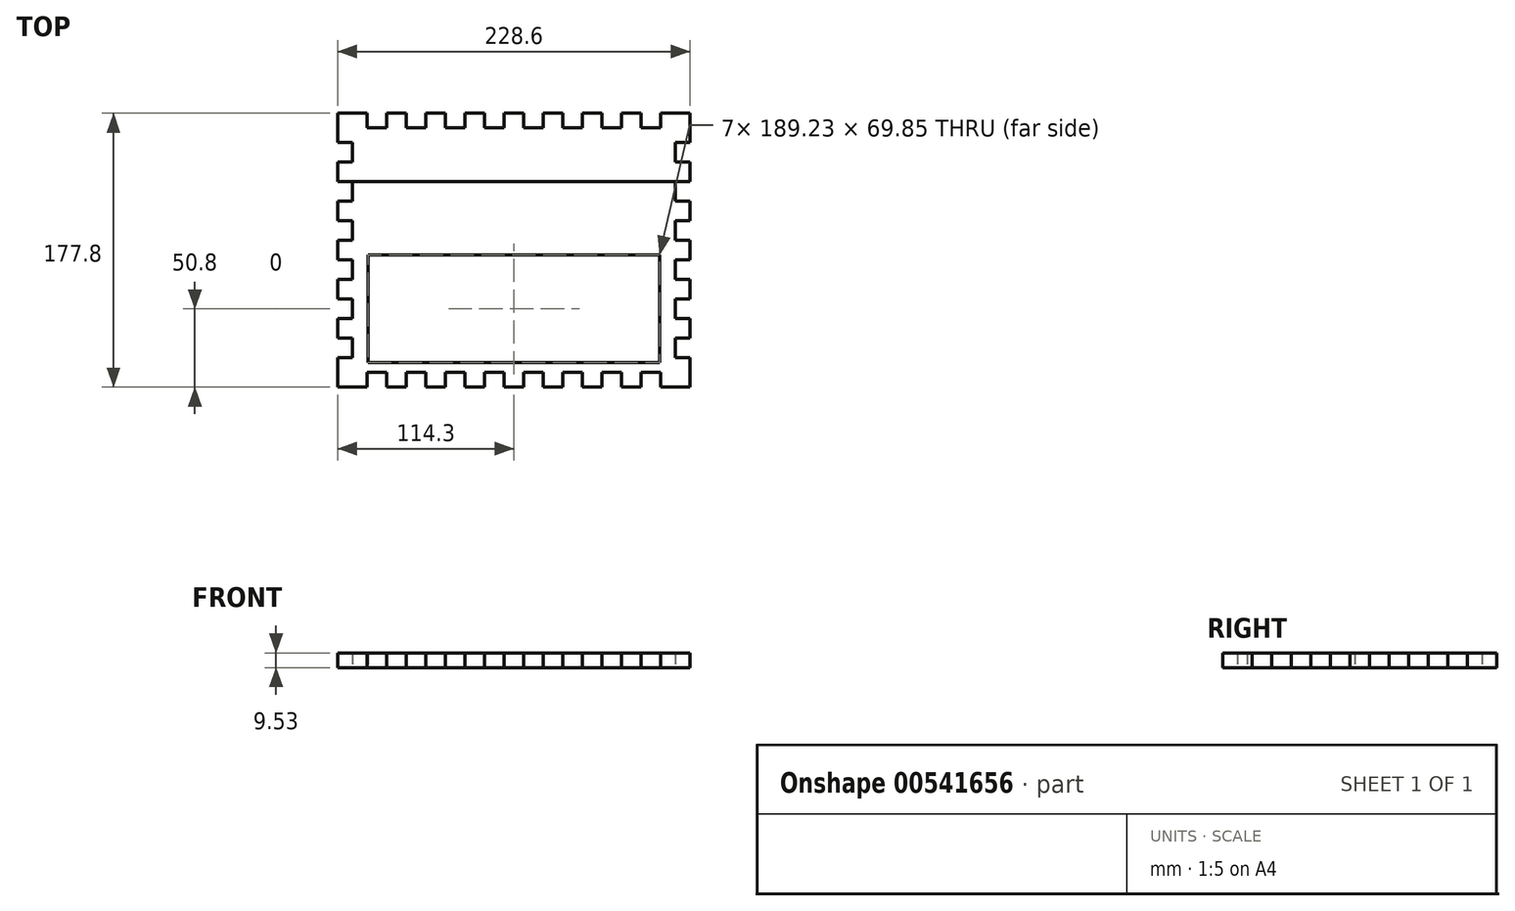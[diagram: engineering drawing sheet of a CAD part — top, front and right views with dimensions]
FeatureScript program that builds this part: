
annotation { "Feature Type Name" : "Feature", "Feature Type Description" : "" }
export const myFeature = defineFeature(function(context is Context, id is Id, definition is map)
    precondition{}
    {
        {
            var Q0;
            Q0=qCreatedBy(makeId("Top.planeOp"),FACE);
            var sketch = newSketch(context, id + "F0", { "sketchPlane" : qUnion([Q0])});
            skLineSegment(sketch, "E0.bottom", {"start": v(0, 0) * mm, "end": v(19.05, 0) * mm});
            skLineSegment(sketch, "E0.left", {"start": v(0, 0) * mm, "end": v(0, -19.05) * mm});
            skLineSegment(sketch, "E1", {"start": v(19.05, 0) * mm, "end": v(19.05, -9.53) * mm});
            skLineSegment(sketch, "E2", {"start": v(19.05, -9.53) * mm, "end": v(31.75, -9.53) * mm});
            skLineSegment(sketch, "E3", {"start": v(31.75, -9.53) * mm, "end": v(31.75, 0) * mm});
            skLineSegment(sketch, "E4", {"start": v(31.75, 0) * mm, "end": v(44.45, 0) * mm});
            skLineSegment(sketch, "E5", {"start": v(44.45, 0) * mm, "end": v(44.45, -9.52) * mm});
            skLineSegment(sketch, "E6", {"start": v(44.45, -9.52) * mm, "end": v(57.15, -9.52) * mm});
            skLineSegment(sketch, "E7", {"start": v(57.15, -9.52) * mm, "end": v(57.15, 0) * mm});
            skLineSegment(sketch, "E8.trimOffspring", {"start": v(57.15, 0) * mm, "end": v(69.85, 0) * mm});
            skLineSegment(sketch, "E9", {"start": v(69.85, 0) * mm, "end": v(69.85, -9.52) * mm});
            skLineSegment(sketch, "E10", {"start": v(69.85, -9.52) * mm, "end": v(82.55, -9.52) * mm});
            skLineSegment(sketch, "E11", {"start": v(82.55, -9.52) * mm, "end": v(82.55, 0) * mm});
            skLineSegment(sketch, "E12", {"start": v(82.55, 0) * mm, "end": v(95.25, 0) * mm});
            skLineSegment(sketch, "E13", {"start": v(95.25, 0) * mm, "end": v(95.25, -9.52) * mm});
            skLineSegment(sketch, "E14", {"start": v(95.25, -9.52) * mm, "end": v(107.95, -9.52) * mm});
            skLineSegment(sketch, "E15", {"start": v(107.95, -9.52) * mm, "end": v(107.95, 0) * mm});
            skLineSegment(sketch, "E16", {"start": v(107.95, 0) * mm, "end": v(120.65, 0) * mm});
            skLineSegment(sketch, "E17", {"start": v(120.65, 0) * mm, "end": v(120.65, -9.52) * mm});
            skLineSegment(sketch, "E18", {"start": v(120.65, -9.52) * mm, "end": v(133.35, -9.52) * mm});
            skLineSegment(sketch, "E19", {"start": v(133.35, -9.52) * mm, "end": v(133.35, 0) * mm});
            skLineSegment(sketch, "E20.trimOffspring", {"start": v(133.35, 0) * mm, "end": v(146.05, 0) * mm});
            skLineSegment(sketch, "E21", {"start": v(146.05, 0) * mm, "end": v(146.05, -9.53) * mm});
            skLineSegment(sketch, "E22", {"start": v(146.05, -9.52) * mm, "end": v(158.75, -9.52) * mm});
            skLineSegment(sketch, "E23", {"start": v(158.75, -9.53) * mm, "end": v(158.75, 0) * mm});
            skLineSegment(sketch, "E24", {"start": v(158.75, 0) * mm, "end": v(171.45, 0) * mm});
            skLineSegment(sketch, "E25", {"start": v(171.45, 0) * mm, "end": v(171.45, -9.52) * mm});
            skLineSegment(sketch, "E26", {"start": v(171.45, -9.52) * mm, "end": v(184.15, -9.52) * mm});
            skLineSegment(sketch, "E27", {"start": v(184.15, -9.52) * mm, "end": v(184.15, 0) * mm});
            skLineSegment(sketch, "E28", {"start": v(184.15, 0) * mm, "end": v(196.85, 0) * mm});
            skLineSegment(sketch, "E29", {"start": v(196.85, 0) * mm, "end": v(196.85, -9.52) * mm});
            skLineSegment(sketch, "E30", {"start": v(196.85, -9.52) * mm, "end": v(209.55, -9.52) * mm});
            skLineSegment(sketch, "E31", {"start": v(209.55, -9.52) * mm, "end": v(209.55, 0) * mm});
            skLineSegment(sketch, "E32.trimOffspring", {"start": v(209.55, 0) * mm, "end": v(228.6, 0) * mm});
            skLineSegment(sketch, "E33", {"start": v(0, -19.05) * mm, "end": v(9.52, -19.05) * mm});
            skLineSegment(sketch, "E34", {"start": v(9.52, -19.05) * mm, "end": v(9.52, -31.75) * mm});
            skLineSegment(sketch, "E35", {"start": v(9.52, -31.75) * mm, "end": v(0, -31.75) * mm});
            skLineSegment(sketch, "E36", {"start": v(0, -31.75) * mm, "end": v(0, -44.45) * mm});
            skLineSegment(sketch, "E37", {"start": v(0, -44.45) * mm, "end": v(9.52, -44.45) * mm});
            skLineSegment(sketch, "E38", {"start": v(9.52, -44.45) * mm, "end": v(9.52, -57.15) * mm});
            skLineSegment(sketch, "E39", {"start": v(9.52, -57.15) * mm, "end": v(0, -57.15) * mm});
            skLineSegment(sketch, "E40", {"start": v(0, -57.15) * mm, "end": v(0, -69.85) * mm});
            skLineSegment(sketch, "E41", {"start": v(0, -69.85) * mm, "end": v(9.52, -69.85) * mm});
            skLineSegment(sketch, "E42", {"start": v(9.53, -69.85) * mm, "end": v(9.53, -82.55) * mm});
            skLineSegment(sketch, "E43", {"start": v(9.53, -82.55) * mm, "end": v(0, -82.55) * mm});
            skLineSegment(sketch, "E44.trimOffspring", {"start": v(0, -82.55) * mm, "end": v(0, -95.25) * mm});
            skLineSegment(sketch, "E45", {"start": v(0, -95.25) * mm, "end": v(9.53, -95.25) * mm});
            skLineSegment(sketch, "E46", {"start": v(9.53, -95.25) * mm, "end": v(9.53, -107.95) * mm});
            skLineSegment(sketch, "E47", {"start": v(9.53, -107.95) * mm, "end": v(0, -107.95) * mm});
            skLineSegment(sketch, "E48", {"start": v(0, -107.95) * mm, "end": v(0, -120.65) * mm});
            skLineSegment(sketch, "E49", {"start": v(0, -120.65) * mm, "end": v(9.53, -120.65) * mm});
            skLineSegment(sketch, "E50", {"start": v(9.53, -120.65) * mm, "end": v(9.53, -133.35) * mm});
            skLineSegment(sketch, "E51", {"start": v(9.53, -133.35) * mm, "end": v(0, -133.35) * mm});
            skLineSegment(sketch, "E52", {"start": v(0, -133.35) * mm, "end": v(0, -146.05) * mm});
            skLineSegment(sketch, "E53", {"start": v(0, -146.05) * mm, "end": v(9.53, -146.05) * mm});
            skLineSegment(sketch, "E54", {"start": v(9.53, -146.05) * mm, "end": v(9.53, -158.75) * mm});
            skLineSegment(sketch, "E55", {"start": v(9.53, -158.75) * mm, "end": v(0, -158.75) * mm});
            skLineSegment(sketch, "E56.trimOffspring", {"start": v(0, -158.75) * mm, "end": v(0, -177.8) * mm});
            skLineSegment(sketch, "E57", {"start": v(114.3, 0) * mm, "end": v(114.3, -38.19) * mm, "construction": true});
            skLineSegment(sketch, "E58", {"start": v(0, -88.9) * mm, "end": v(48.13, -88.9) * mm, "construction": true});
            skLineSegment(sketch, "E59.MirrorCS", {"start": v(228.6, 0) * mm, "end": v(228.6, -19.05) * mm});
            skLineSegment(sketch, "E60.MirrorCS", {"start": v(228.6, -19.05) * mm, "end": v(219.08, -19.05) * mm});
            skLineSegment(sketch, "E61.MirrorCS", {"start": v(219.08, -19.05) * mm, "end": v(219.08, -31.75) * mm});
            skLineSegment(sketch, "E62.MirrorCS", {"start": v(219.08, -31.75) * mm, "end": v(228.6, -31.75) * mm});
            skLineSegment(sketch, "E63.MirrorCS", {"start": v(228.6, -31.75) * mm, "end": v(228.6, -44.45) * mm});
            skLineSegment(sketch, "E64.MirrorCS", {"start": v(228.6, -44.45) * mm, "end": v(219.08, -44.45) * mm});
            skLineSegment(sketch, "E65.MirrorCS", {"start": v(219.08, -44.45) * mm, "end": v(219.08, -57.15) * mm});
            skLineSegment(sketch, "E66.MirrorCS", {"start": v(219.08, -57.15) * mm, "end": v(228.6, -57.15) * mm});
            skLineSegment(sketch, "E67.MirrorCS", {"start": v(228.6, -57.15) * mm, "end": v(228.6, -69.85) * mm});
            skLineSegment(sketch, "E68.MirrorCS", {"start": v(219.08, -69.85) * mm, "end": v(219.08, -82.55) * mm});
            skLineSegment(sketch, "E69.MirrorCS", {"start": v(219.08, -82.55) * mm, "end": v(228.6, -82.55) * mm});
            skLineSegment(sketch, "E70.MirrorCS", {"start": v(228.6, -82.55) * mm, "end": v(228.6, -95.25) * mm});
            skLineSegment(sketch, "E71.MirrorCS", {"start": v(228.6, -95.25) * mm, "end": v(219.08, -95.25) * mm});
            skLineSegment(sketch, "E72.MirrorCS", {"start": v(219.08, -95.25) * mm, "end": v(219.08, -107.95) * mm});
            skLineSegment(sketch, "E73.MirrorCS", {"start": v(219.08, -107.95) * mm, "end": v(228.6, -107.95) * mm});
            skLineSegment(sketch, "E74.MirrorCS", {"start": v(228.6, -107.95) * mm, "end": v(228.6, -120.65) * mm});
            skLineSegment(sketch, "E75.MirrorCS", {"start": v(228.6, -120.65) * mm, "end": v(219.08, -120.65) * mm});
            skLineSegment(sketch, "E76.MirrorCS", {"start": v(219.08, -120.65) * mm, "end": v(219.08, -133.35) * mm});
            skLineSegment(sketch, "E77.MirrorCS", {"start": v(219.08, -133.35) * mm, "end": v(228.6, -133.35) * mm});
            skLineSegment(sketch, "E78.MirrorCS", {"start": v(228.6, -133.35) * mm, "end": v(228.6, -146.05) * mm});
            skLineSegment(sketch, "E79.MirrorCS", {"start": v(228.6, -146.05) * mm, "end": v(219.08, -146.05) * mm});
            skLineSegment(sketch, "E80.MirrorCS", {"start": v(219.08, -146.05) * mm, "end": v(219.08, -158.75) * mm});
            skLineSegment(sketch, "E81.MirrorCS", {"start": v(219.08, -158.75) * mm, "end": v(228.6, -158.75) * mm});
            skLineSegment(sketch, "E82.MirrorCS", {"start": v(228.6, -158.75) * mm, "end": v(228.6, -177.8) * mm});
            skLineSegment(sketch, "E83.MirrorCS", {"start": v(0, -177.8) * mm, "end": v(19.05, -177.8) * mm});
            skLineSegment(sketch, "E84.MirrorCS", {"start": v(19.05, -177.8) * mm, "end": v(19.05, -168.28) * mm});
            skLineSegment(sketch, "E85.MirrorCS", {"start": v(19.05, -168.28) * mm, "end": v(31.75, -168.28) * mm});
            skLineSegment(sketch, "E86.MirrorCS", {"start": v(31.75, -168.28) * mm, "end": v(31.75, -177.8) * mm});
            skLineSegment(sketch, "E87.MirrorCS", {"start": v(31.75, -177.8) * mm, "end": v(44.45, -177.8) * mm});
            skLineSegment(sketch, "E88.MirrorCS", {"start": v(44.45, -168.28) * mm, "end": v(57.15, -168.28) * mm});
            skLineSegment(sketch, "E89.MirrorCS", {"start": v(57.15, -168.28) * mm, "end": v(57.15, -177.8) * mm});
            skLineSegment(sketch, "E90.MirrorCS", {"start": v(57.15, -177.8) * mm, "end": v(69.85, -177.8) * mm});
            skLineSegment(sketch, "E91.MirrorCS", {"start": v(44.45, -177.8) * mm, "end": v(44.45, -168.28) * mm});
            skLineSegment(sketch, "E92.MirrorCS", {"start": v(69.85, -177.8) * mm, "end": v(69.85, -168.28) * mm});
            skLineSegment(sketch, "E93.MirrorCS", {"start": v(69.85, -168.28) * mm, "end": v(82.55, -168.28) * mm});
            skLineSegment(sketch, "E94.MirrorCS", {"start": v(82.55, -168.28) * mm, "end": v(82.55, -177.8) * mm});
            skLineSegment(sketch, "E95.MirrorCS", {"start": v(82.55, -177.8) * mm, "end": v(95.25, -177.8) * mm});
            skLineSegment(sketch, "E96.MirrorCS", {"start": v(95.25, -177.8) * mm, "end": v(95.25, -168.28) * mm});
            skLineSegment(sketch, "E97.MirrorCS", {"start": v(95.25, -168.28) * mm, "end": v(107.95, -168.28) * mm});
            skLineSegment(sketch, "E98.MirrorCS", {"start": v(107.95, -168.28) * mm, "end": v(107.95, -177.8) * mm});
            skLineSegment(sketch, "E99.MirrorCS", {"start": v(120.65, -177.8) * mm, "end": v(120.65, -168.28) * mm});
            skLineSegment(sketch, "E100.MirrorCS", {"start": v(120.65, -168.28) * mm, "end": v(133.35, -168.28) * mm});
            skLineSegment(sketch, "E101.MirrorCS", {"start": v(133.35, -168.28) * mm, "end": v(133.35, -177.8) * mm});
            skLineSegment(sketch, "E102.MirrorCS", {"start": v(133.35, -177.8) * mm, "end": v(146.05, -177.8) * mm});
            skLineSegment(sketch, "E103.MirrorCS", {"start": v(146.05, -177.8) * mm, "end": v(146.05, -168.28) * mm});
            skLineSegment(sketch, "E104.MirrorCS", {"start": v(146.05, -168.28) * mm, "end": v(158.75, -168.28) * mm});
            skLineSegment(sketch, "E105.MirrorCS", {"start": v(158.75, -168.28) * mm, "end": v(158.75, -177.8) * mm});
            skLineSegment(sketch, "E106.MirrorCS", {"start": v(158.75, -177.8) * mm, "end": v(171.45, -177.8) * mm});
            skLineSegment(sketch, "E107.MirrorCS", {"start": v(171.45, -177.8) * mm, "end": v(171.45, -168.28) * mm});
            skLineSegment(sketch, "E108.MirrorCS", {"start": v(171.45, -168.28) * mm, "end": v(184.15, -168.28) * mm});
            skLineSegment(sketch, "E109.MirrorCS", {"start": v(184.15, -168.28) * mm, "end": v(184.15, -177.8) * mm});
            skLineSegment(sketch, "E110.MirrorCS", {"start": v(184.15, -177.8) * mm, "end": v(196.85, -177.8) * mm});
            skLineSegment(sketch, "E111.MirrorCS", {"start": v(196.85, -177.8) * mm, "end": v(196.85, -168.28) * mm});
            skLineSegment(sketch, "E112.MirrorCS", {"start": v(196.85, -168.28) * mm, "end": v(209.55, -168.28) * mm});
            skLineSegment(sketch, "E113.MirrorCS", {"start": v(209.55, -168.28) * mm, "end": v(209.55, -177.8) * mm});
            skLineSegment(sketch, "E114.MirrorCS", {"start": v(209.55, -177.8) * mm, "end": v(228.6, -177.8) * mm});
            skLineSegment(sketch, "E115.MirrorCS", {"start": v(107.95, -177.8) * mm, "end": v(120.65, -177.8) * mm});
            skLineSegment(sketch, "E116.MirrorCS", {"start": v(228.6, -69.85) * mm, "end": v(219.08, -69.85) * mm});
            skLineSegment(sketch, "E117", {"start": v(9.52, -44.45) * mm, "end": v(219.08, -44.45) * mm});
            skLineSegment(sketch, "E118.bottom", {"start": v(19.69, -92.07) * mm, "end": v(208.92, -92.07) * mm});
            skLineSegment(sketch, "E118.top", {"start": v(19.69, -161.93) * mm, "end": v(208.92, -161.93) * mm});
            skLineSegment(sketch, "E118.left", {"start": v(19.69, -92.07) * mm, "end": v(19.69, -161.93) * mm});
            skLineSegment(sketch, "E118.right", {"start": v(208.92, -92.07) * mm, "end": v(208.92, -161.93) * mm});
            skSolve(sketch);
        }
        {
            var Q0;
            Q0=makeQuery(id+"F0.imprint","IMPRINT",FACE,{"disambiguationData":[TD([[makeQuery(id+"F0.imprint","IMPRINT",EDGE,{"derivedFrom":sQuery(id+"F0.wireOp",EDGE,"E0.bottom")}),-1.0]])]});
            extrude(context, id + "F1", {"entities" : qUnion([Q0]), "depth" : 9.52 * mm, "offsetDistance" : 25.4 * mm});
        }
        {
            var Q0;
            Q0=makeQuery(id+"F0.imprint","IMPRINT",FACE,{"disambiguationData":[TD([[makeQuery(id+"F0.imprint","IMPRINT",EDGE,{"derivedFrom":sQuery(id+"F0.wireOp",EDGE,"E38")}),1.0]])]});
            extrude(context, id + "F2", {"entities" : qUnion([Q0]), "depth" : 9.52 * mm, "offsetDistance" : 25.4 * mm});
        }
    });
